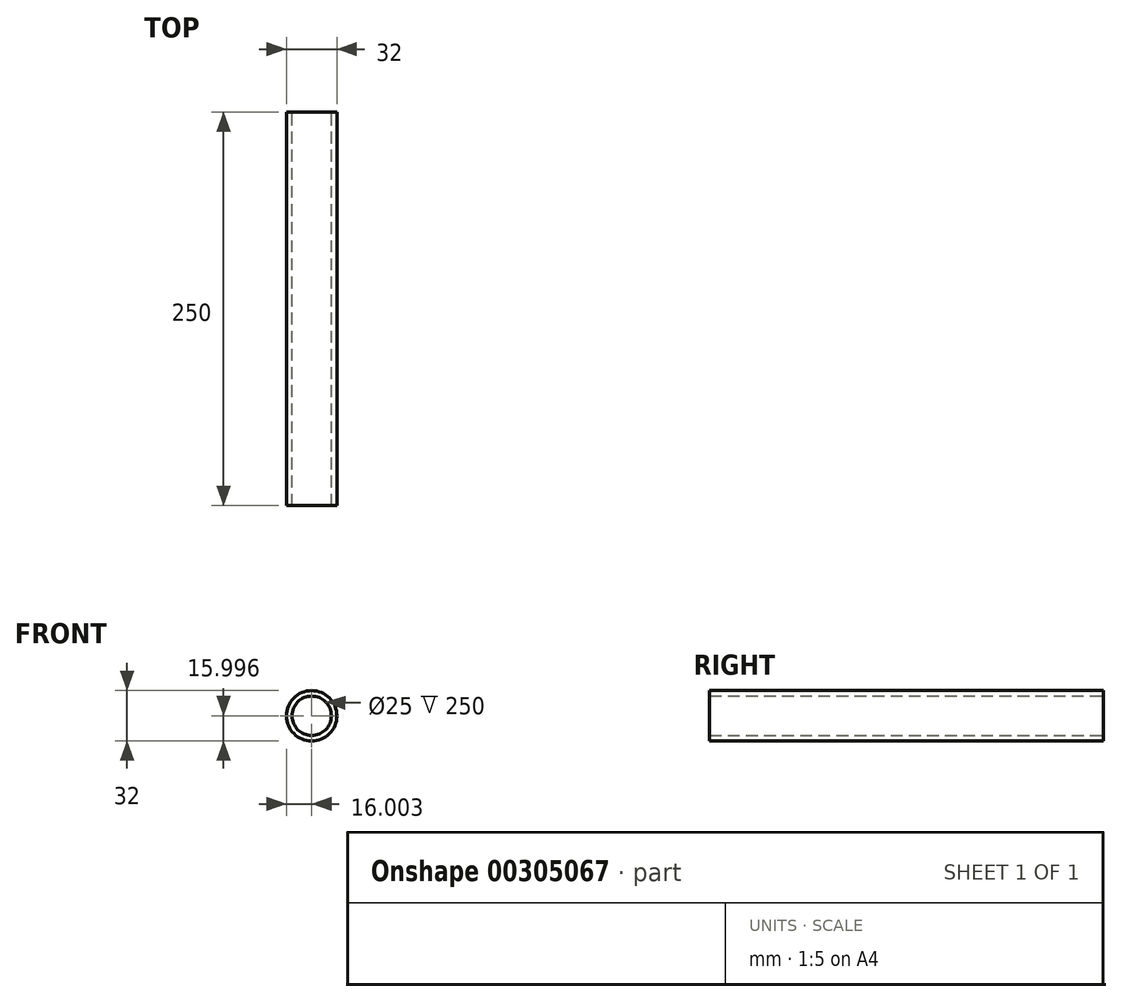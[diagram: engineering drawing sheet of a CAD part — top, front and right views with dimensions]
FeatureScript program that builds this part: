
annotation { "Feature Type Name" : "Feature", "Feature Type Description" : "" }
export const myFeature = defineFeature(function(context is Context, id is Id, definition is map)
    precondition{}
    {
        {
            var Q0;
            Q0=qCreatedBy(makeId("Front.planeOp"),FACE);
            var sketch = newSketch(context, id + "F0", { "sketchPlane" : qUnion([Q0])});
            skCircle(sketch, "E0", {"center": v(-51.57, 33.57) * mm, "radius": 12.5 * mm});
            skCircle(sketch, "E1.0", {"center": v(-51.57, 33.57) * mm, "radius": 16 * mm});
            skSolve(sketch);
        }
        {
            var Q0;
            Q0 = qSketchRegion(id + "F0", true);
            extrude(context, id + "F1", {"entities" : qUnion([Q0]), "flatOperationType" : FlatOperationType.REMOVE, "offsetDistance" : 25 * mm, "depth" : 250 * mm, "domain" : OperationDomain.MODEL});
        }
    });
